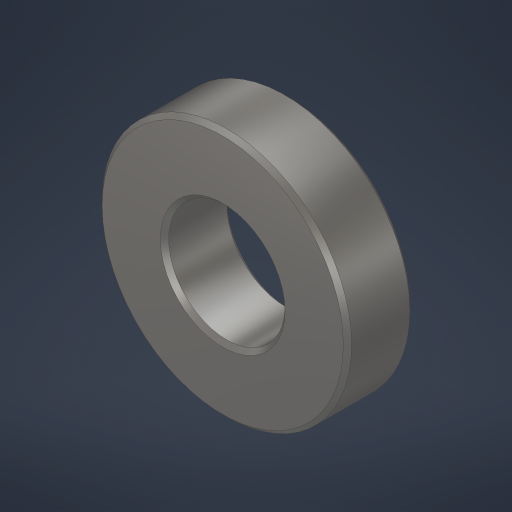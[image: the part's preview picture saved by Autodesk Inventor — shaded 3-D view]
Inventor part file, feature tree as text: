
AUTODESK INVENTOR PART (.ipt)
format: ipt  version: 2023.4 (Build 274418000, 418)  size: 200,704 bytes
history: native  units: in
note: dims shown in document units (in); Inventor stores cm internally (conversion verified against a paired STEP export)
features: extrude x1, chamfer x1
ambient origin geometry x8: Origin, YZ Plane, XZ Plane, XY Plane, X Axis, Y Axis, Z Axis, Center Point
bodies: Solid1 (feature_tree)
feature tree (2):
  extrude  "Extrusion1"  Depth=1.875in
  chamfer  "Chamfer1"  Distance=0.875in
